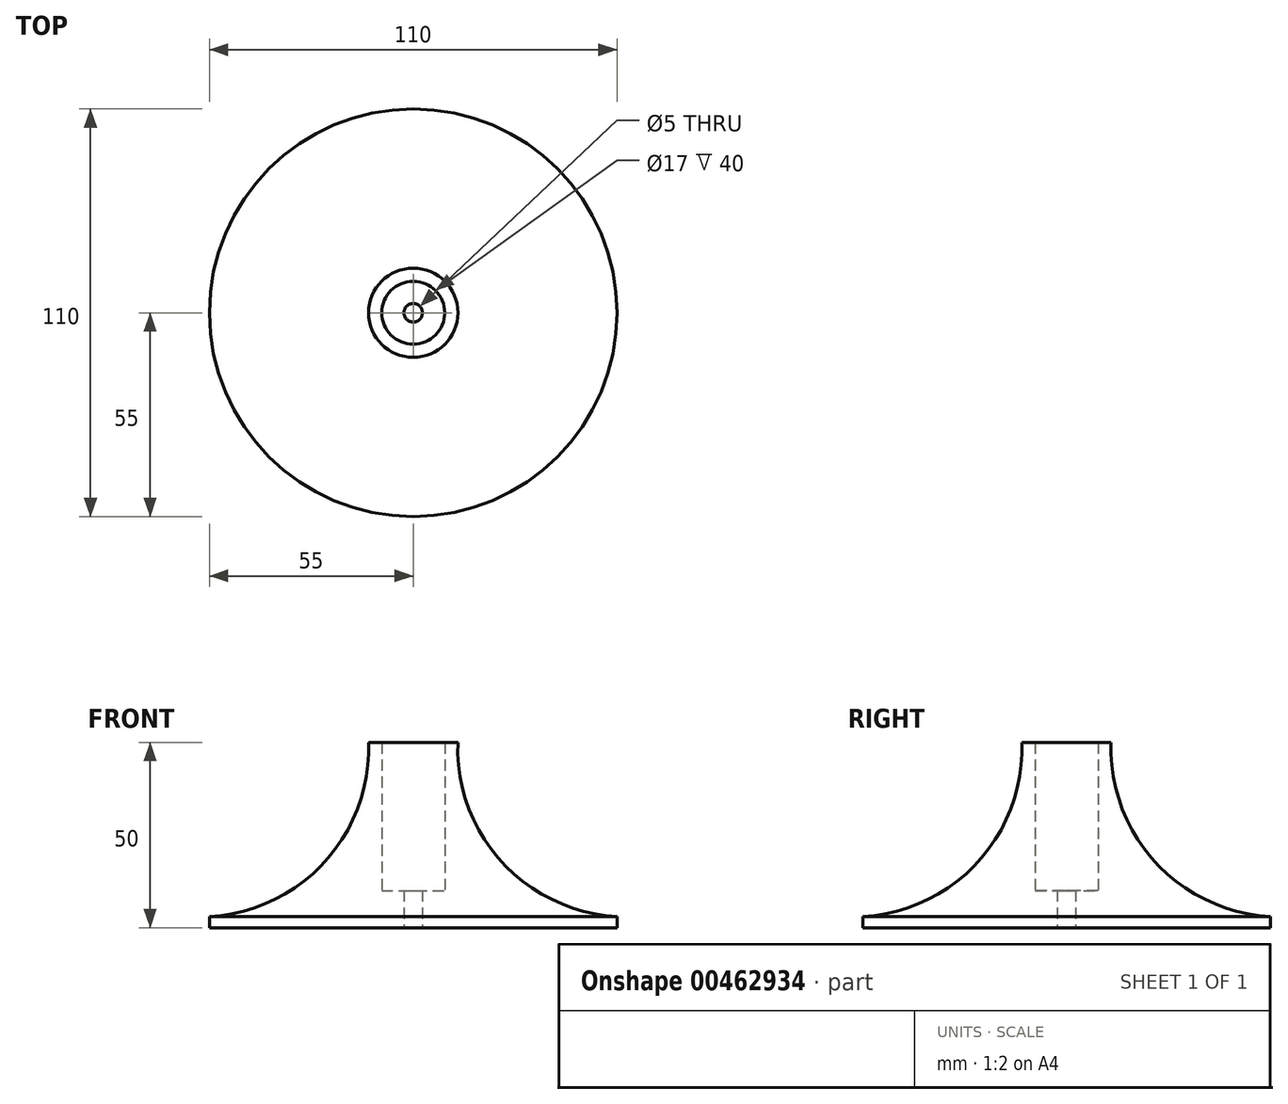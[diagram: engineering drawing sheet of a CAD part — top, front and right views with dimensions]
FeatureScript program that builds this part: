
annotation { "Feature Type Name" : "Feature", "Feature Type Description" : "" }
export const myFeature = defineFeature(function(context is Context, id is Id, definition is map)
    precondition{}
    {
        {
            var Q0;
            Q0=qCreatedBy(makeId("Front.planeOp"),FACE);
            var sketch = newSketch(context, id + "F0", { "sketchPlane" : qUnion([Q0])});
            skLineSegment(sketch, "E0", {"start": v(0, 0) * mm, "end": v(0, 50) * mm, "construction": true});
            skLineSegment(sketch, "E1", {"start": v(0, 0) * mm, "end": v(-55, 0) * mm, "construction": true});
            skLineSegment(sketch, "E2", {"start": v(-55, 0) * mm, "end": v(-55, 3) * mm});
            skLineSegment(sketch, "E3", {"start": v(-2.5, 0) * mm, "end": v(-2.5, 10) * mm});
            skLineSegment(sketch, "E4", {"start": v(-2.5, 10) * mm, "end": v(-8.5, 10) * mm});
            skLineSegment(sketch, "E5", {"start": v(-8.5, 10) * mm, "end": v(-8.5, 50) * mm});
            skLineSegment(sketch, "E6", {"start": v(-2.5, 0) * mm, "end": v(-55, 0) * mm});
            skLineSegment(sketch, "E7", {"start": v(-8.5, 50) * mm, "end": v(-12.04, 50) * mm});
            skArc(sketch, "E8", {"start": v(-55, 3) * mm, "mid": v(-23.92, 17.72) * mm, "end": v(-12.04, 50) * mm});
            skSolve(sketch);
        }
        {
            var Q0;
            Q0 = qSketchRegion(id + "F0", true);
            var Q1;
            Q1=sQuery(id+"F0.wireOp",EDGE,"E0");
            revolve(context, id + "F1", {"entities" : qUnion([Q0]), "axis" : qUnion([Q1]), "revolveType" : RevolveType.FULL});
        }
    });
